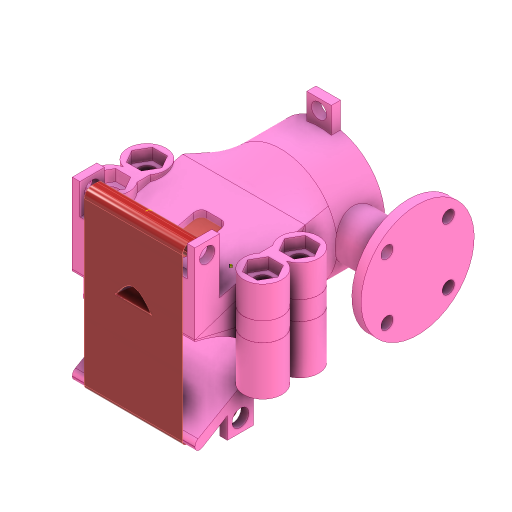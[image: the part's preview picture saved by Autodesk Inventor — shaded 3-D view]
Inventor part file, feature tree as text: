
AUTODESK INVENTOR PART (.ipt)
format: ipt  version: 2024 (Build 280153000, 153)  size: 1,844,736 bytes
history: native  units: mm
features: sketch x24, extrude x19, projected_geometry x11, split x10, other x10, loft x6, boolean_combine x5, plane x4, fillet x2, sweep x2, thicken_offset x2
ambient origin geometry x8: Origin, YZ Plane, XZ Plane, XY Plane, X Axis, Y Axis, Z Axis, Center Point
bodies: Solid1 (feature_tree), Solid2 (feature_tree), Solid19 (feature_tree), Solid20 (feature_tree), Solid21 (feature_tree), Solid22 (feature_tree), Solid23 (feature_tree), Solid3 (feature_tree), Solid4 (feature_tree), Solid5 (feature_tree), Solid6 (feature_tree), Solid7 (feature_tree), Solid8 (feature_tree), Solid9 (feature_tree), Solid10 (feature_tree), Solid11 (feature_tree), Solid12 (feature_tree), Solid13 (feature_tree), Solid14 (feature_tree), Solid15 (feature_tree), Solid16 (feature_tree), Solid17 (feature_tree), Solid18 (feature_tree)
feature tree (95):
  extrude  "Extrusion1"  Depth=3.0mm TaperAngle=0.0deg
  extrude  "Extrusion2"  Depth=3.0mm TaperAngle=0.0deg
  extrude  "Extrusion3"  Depth=40.0mm
  plane  "Work Plane2"
  sketch  "Sketch4"  dims[d4=29.0mm d5=3.0mm d6=0.0mm]
  loft  "Loft1"
  loft  "Loft2"
  loft  "Loft3"
  loft  "Loft4"
  boolean_combine  "Combine1"
  loft  "Loft5"
  fillet  "Fillet1"  [1 undecoded]
  fillet  "Fillet2"  [1 undecoded]
  plane  "Work Plane3"
  extrude  "Extrusion5"  TaperAngle=0.0deg  [1 undecoded]
  extrude  "Extrusion6"  TaperAngle=0.0deg  [1 undecoded]
  extrude  "Extrusion7"  Depth=40.0mm
  extrude  "Extrusion8"  TaperAngle=0.0deg  [1 undecoded]
  extrude  "Extrusion9"  Depth=2.0mm
  extrude  "Extrusion10"  Depth=38.0mm
  extrude  "Extrusion11"  Depth=3.0mm TaperAngle=0.0deg
  extrude  "Extrusion12"  Depth=3.0mm TaperAngle=0.0deg
  extrude  "Extrusion13"  Depth=12.5mm TaperAngle=0.0deg
  extrude  "Extrusion14"  Depth=3.7mm TaperAngle=0.0deg
  extrude  "Extrusion15"  Depth=8.5mm
  split  "Split1"
  split  "Split2"
  split  "Split3"
  split  "Split4"
  split  "Split5"
  split  "Split6"
  split  "Split7"
  boolean_combine  "Combine2"
  split  "Split8"
  boolean_combine  "Combine3"
  boolean_combine  "Combine4"
  extrude  "Extrusion16"  Depth=8.5mm
  extrude  "Extrusion17"  Depth=2.7mm TaperAngle=0.0deg
  sketch  "Sketch36"  dims[d47=15.0mm d48=3.0mm d49=0.0mm]
  sweep  "Sweep1"
  split  "Split9"
  loft  "Loft6"
  thicken_offset  "Thicken1"
  extrude  "Extrusion18"  Depth=10.0mm TaperAngle=0.0deg
  sweep  "Sweep2"
  split  "Split10"
  thicken_offset  "Thicken2"
  boolean_combine  "Combine5"
  plane  "Work Plane4"
  extrude  "Extrusion19"  Depth=10.0mm
  other  "Work Point1"
  other  "Work Point2"
  other  "Work Point3"
  extrude  "Extrusion20"  Depth=10.0mm
  sketch  "Sketch1"  dims[d0=3.0mm d1=0.0mm d2=9.5mm d3=0.0mm]
  plane  "Work Plane1"
  other  "2D Equation Curve1"
  other  "Edges1"
  other  "Edges2"
  other  "Edges3"
  other  "Edges4"
  sketch  "Sketch7"  dims[d7=12.0mm d8=36.0mm d9=40.0mm]
  sketch  "Sketch10"  dims[d10=9.0mm d11=10.0mm]
  sketch  "Sketch12"  dims[d12=3.0mm d13=-6.0mm d14=6.0mm]
  sketch  "Sketch13"  dims[d15=40.0mm d16=26.0mm]
  sketch  "Sketch16"  dims[d17=20.0mm d18=20.0mm]
  projected_geometry  "Projected Loop1"
  sketch  "Sketch18"  dims[d19=0.0mm d20=90.0deg d21=0.0mm d22=90.0deg d23=0.0mm d24=90.0deg d25=0.0mm d26=90.0deg]
  sketch  "Sketch19"  dims[d27=0.0mm d28=90.0deg d29=0.0mm d30=90.0deg]
  projected_geometry  "Projected Loop2"
  projected_geometry  "Projected Loop3"
  projected_geometry  "Projected Loop4"
  projected_geometry  "Projected Loop5"
  sketch  "Sketch23"  dims[d31=0.0mm d32=90.0deg d33=0.0mm d34=90.0deg]
  sketch  "Sketch24"  dims[d35=26.0mm d36=40.0mm]
  sketch  "Sketch28"  dims[d37=4.0mm d38=0.0mm d39=90.0deg]
  sketch  "Sketch29"  dims[d40=0.0mm d41=90.0deg d42=2.0mm]
  sketch  "Sketch35"  dims[d43=1.5mm d46=38.0mm]
  projected_geometry  "Projected Loop11"
  sketch  "3D Sketch2"
  other  "Srf1"
  sketch  "Sketch38"  dims[d50=15.0mm d51=3.0mm d52=0.0mm]
  projected_geometry  "Projected Loop12"
  sketch  "Sketch42"  dims[d53=11.0mm d54=12.5mm d55=0.0mm]
  projected_geometry  "Projected Loop19"
  projected_geometry  "Projected Loop20"
  sketch  "Sketch43"  dims[d56=11.0mm d57=3.7mm d58=0.0mm]
  sketch  "Sketch46"  dims[d59=20.0mm d60=0.0mm d61=8.5mm]
  projected_geometry  "Projected Loop21"
  sketch  "3D Sketch3"
  sketch  "Sketch47"  dims[d62=8.5mm d63=8.5mm]
  projected_geometry  "Projected Loop22"
  sketch  "Sketch49"  dims[d64=8.5mm d65=2.7mm d66=0.0mm]
  sketch  "Sketch50"  dims[d67=40.0mm d68=10.0mm d69=2.7mm d70=0.0mm d71=2.5mm d72=0.0mm d73=2.5mm d74=0.0mm d75=9.0mm d76=2.0mm d77=0.0mm d78=0.0mm d79=7.0mm d80=5.5mm d81=8.5mm d82=8.5mm d83=2.5mm d84=0.0mm d85=2.5mm d86=0.0mm d87=0.5mm d88=0.0mm d89=0.0mm d91=10.0mm d92=10.0mm d93=0.1mm d94=0.0mm d95=16.0mm d96=2.5mm d97=4.0mm d98=2.5mm d99=2.5mm d100=5.0mm d101=5.0mm d102=2.5mm d103=2.5mm d104=2.5mm d105=2.5mm d106=0.0mm d107=0.0mm d108=2.5mm d109=2.5mm d110=0.0mm d111=90.0deg d112=0.0mm d113=90.0deg d114=0.1mm d115=0.1mm d116=0.1mm d117=0.0mm d118=15.0mm d119=3.0mm d120=1.6mm d121=1.5mm d122=16.5mm d125=5.5mm d126=2.5mm d127=2.5mm d128=0.0mm d129=0.0mm d130=0.1mm d131=0.1mm d132=58.25mm d133=6.0mm d134=16.0mm d135=0.0mm d136=12.0mm d137=12.0mm d138=12.0mm d139=12.0mm d140=10.0mm d141=0.0mm]
  other  "Unwrap1"
note: 5 required parameter values undecoded (feature->parameter linkage not recoverable at this tier; creation-order binding heuristic only, values carry confidence <= 0.55)
